# Revit family: Faucet-Lavatory-KOHLER-Buckley-K-35951
name_source: partatom
category: Plumbing Fixtures
units: mm (PartAtom-declared; Revit-internal decimal feet)

## family parameters
Cut with Voids When Loaded = No
Host = Face
OmniClass Number = 23.31.11.00
OmniClass Title = Faucets
Part Type = Normal
Room Calculation Point = No
Round Connector Dimension = Use Diameter
Shared = No

## types (6) — shared parameters
ADA Compliant = No
Assembly Code = D2010
CW Connection = Yes
Cold Water Inlet = Cold Water Inlet
Date Modified = 11/16/2023
Default Elevation = 36"
Drain Included = No
Faucet Hole Spacing = 4"
Flow Rate = 1 GPM
HW Connection = Yes
Handle Clearance = 3"
Height = 7 3/8"
Hot Water Inlet = Hot Water Inlet
Length = 5"
Manufacturer = Kohler Co.
Master Format 2014 = 22 41 39
Master Format 2014 Name = Residential Faucets, Supplies, and Trim
Material = Premium Metal Construction
Pressure = 0.00 psi
Product Documentation Link = https://www.us.kohler.com
Product Name = Buckley
Product Page URL = http://www.us.kohler.com
Spout Reach = 5"
URL = https://www.us.kohler.com
Vent Connection = No
Waste Connection = No
Waste Water Outlet = Waste Water Outlet
WaterSense Certified = No
Width = 4"

## per-type parameters (varying)
| type | Description | Finish | Model | Type |
| 1.2 GPM, CP-Polished Chrome | Centerset Lavatory Faucet 1.2 GPM | Kohler-Metal-CP-Polished_Chrome | K-35951-4-CP | 1 |
| 1.2 GPM, BN-Vibrant Brushed Nickel | Centerset Lavatory Faucet 1.2 GPM | Kohler-Metal-BN-Vibrant_Brushed_Nickel | K-35951-4-BN | 2 |
| 1.2 GPM, BL-Matte Black | Centerset Lavatory Faucet 1.2 GPM | Kohler-Metal-BL-Matte_Black | K-35951-4-BL | 3 |
| 1.0 GPM, CP-Polished Chrome | Centerset Lavatory Faucet 1.0 GPM | Kohler-Metal-CP-Polished_Chrome | K-35951-4K-CP | 4 |
| 1.0 GPM, BN-Vibrant Brushed Nickel | Centerset Lavatory Faucet 1.0 GPM | Kohler-Metal-BN-Vibrant_Brushed_Nickel | K-35951-4K-BN | 5 |
| 1.0 GPM, BL-Matte Black | Centerset Lavatory Faucet 1.0 GPM | Kohler-Metal-BL-Matte_Black | K-35951-4K-BL | 6 |

## geometry (parser evidence)
native form markers: Sweep x6
no freeform markers — native parametric forms only
